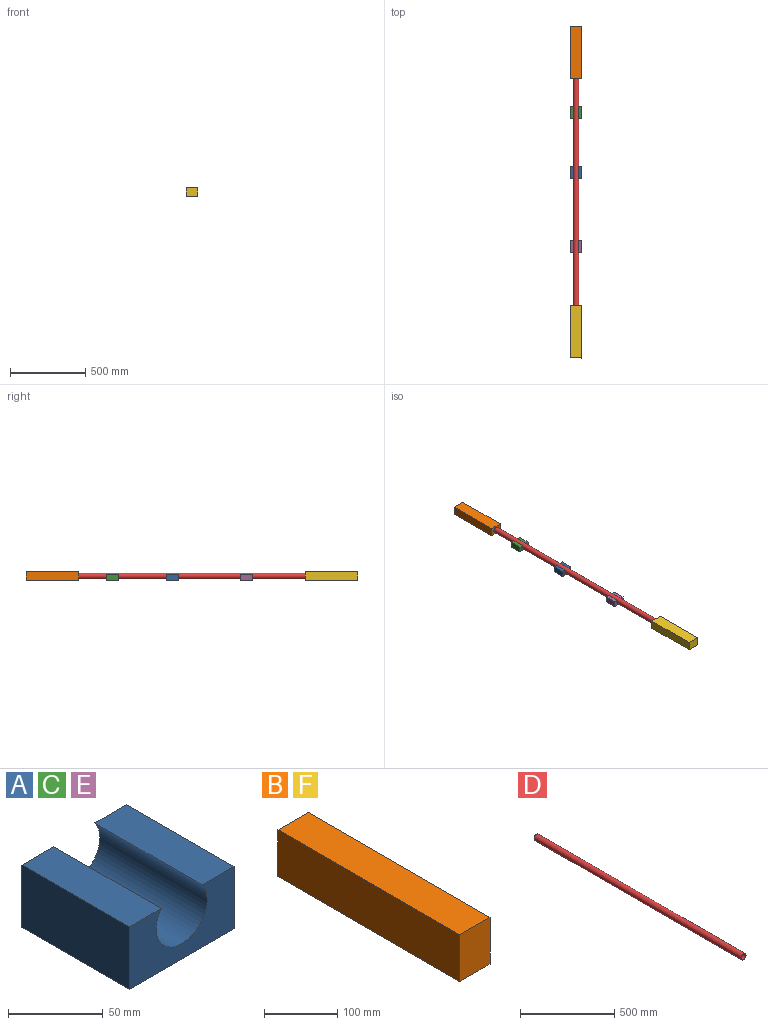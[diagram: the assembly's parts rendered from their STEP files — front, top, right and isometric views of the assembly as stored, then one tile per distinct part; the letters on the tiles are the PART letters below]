
ASSEMBLY  parts=6 mates=6
PART A: 8 faces, bbox 78x80x40.3 mm
  f0: plane 80x40.29mm, normal (-1,0,0), area 3223mm2, adj f2,f3,f4,f6
  f1: plane 80x40.29mm, normal (1,0,0), area 3223mm2, adj f2,f3,f4,f7
  f2: plane 80x78mm, normal (0,0,-1), area 6240mm2, adj f0,f1,f3,f4
  f3: plane 78x40.29mm, normal (0,-1,0), area 2173.2mm2, adj f0,f1,f2,f5,f6,f7
  f4: plane 78x40.29mm, normal (0,1,0), area 2173.2mm2, adj f0,f1,f2,f5,f6,f7
  f5: cylinder r=19mm len=80mm, axis (0,-1,0), area 6709mm2, adj f3,f4,f6,f7
  f6: plane 80x23.72mm, normal (0,0,1), area 1897.3mm2, adj f0,f3,f4,f5
  f7: plane 80x23.72mm, normal (0,0,1), area 1897.3mm2, adj f1,f3,f4,f5
PART B: 8 faces, bbox 58x350x78 mm
  f0: plane 350x58mm, normal (0,0,1), area 20300mm2, adj f1,f3,f4,f5
  f1: plane 78x58mm, normal (0,-1,0), area 4524mm2, adj f0,f2,f4,f5
  f2: plane 350x58mm, normal (0,0,-1), area 20300mm2, adj f1,f3,f4,f5
  f3: plane 78x58mm, normal (0,1,0), area 3389.9mm2, adj f0,f2,f4,f5,f6
  f4: plane 350x78mm, normal (1,0,0), area 27300mm2, adj f0,f1,f2,f3
  f5: plane 350x78mm, normal (-1,0,0), area 27300mm2, adj f0,f1,f2,f3
  f6: cylinder r=19mm len=50mm, axis (0,1,0), area 5969mm2, adj f3,f7
  f7: plane 38x38mm, normal (0,1,0), area 1134.1mm2, adj f6
PART C: same geometry as A
PART D: 4 faces, bbox 38x1550x38 mm
  f0: cylinder r=17.5mm len=1550mm, axis (0,1,0), area 170431.4mm2, adj f2,f3
  f1: cylinder r=19mm len=1550mm, axis (0,1,0), area 185039.8mm2, adj f2,f3
  f2: plane 38x38mm, normal (0,-1,0), area 172mm2, adj f0,f1
  f3: plane 38x38mm, normal (0,1,0), area 172mm2, adj f0,f1
PART E: same geometry as A
PART F: same geometry as B
PLACE A rot(axis=(0.02,0.06,-1),0deg) t=(206.19,1078.33,104.1)mm
PLACE B rot(axis=(0.71,0,0.71),180deg) t=(206.19,1876.6,75.1)mm
PLACE C rot(axis=(0.02,0.06,-1),0deg) t=(206.19,1478.59,104.1)mm
PLACE D rot(axis=(0,1,0),90deg) t=(206.19,946.6,104.1)mm
PLACE E rot(axis=(0.02,0.06,-1),0deg) t=(206.19,589.81,104.1)mm
PLACE F rot(axis=(0,1,0),90deg) t=(206.19,26.6,133.1)mm
MATE slider C.f5 <-> D.f1  axis (0,-1,0) through (206.19,1518.59,104.1)mm
MATE fastened F.f6 <-> B.f6  axis (0,1,0) through (206.19,201.6,104.1)mm
MATE slider D.f1 <-> F.f6  axis (0,1,0) through (206.19,171.6,104.1)mm
MATE slider A.f5 <-> D.f1  axis (0,-1,0) through (206.19,1078.33,104.1)mm
MATE slider E.f5 <-> D.f1  axis (0,-1,0) through (206.19,589.81,104.1)mm
MATE slider B.f6 <-> D.f1  axis (0,-1,0) through (206.19,1701.6,104.1)mm
